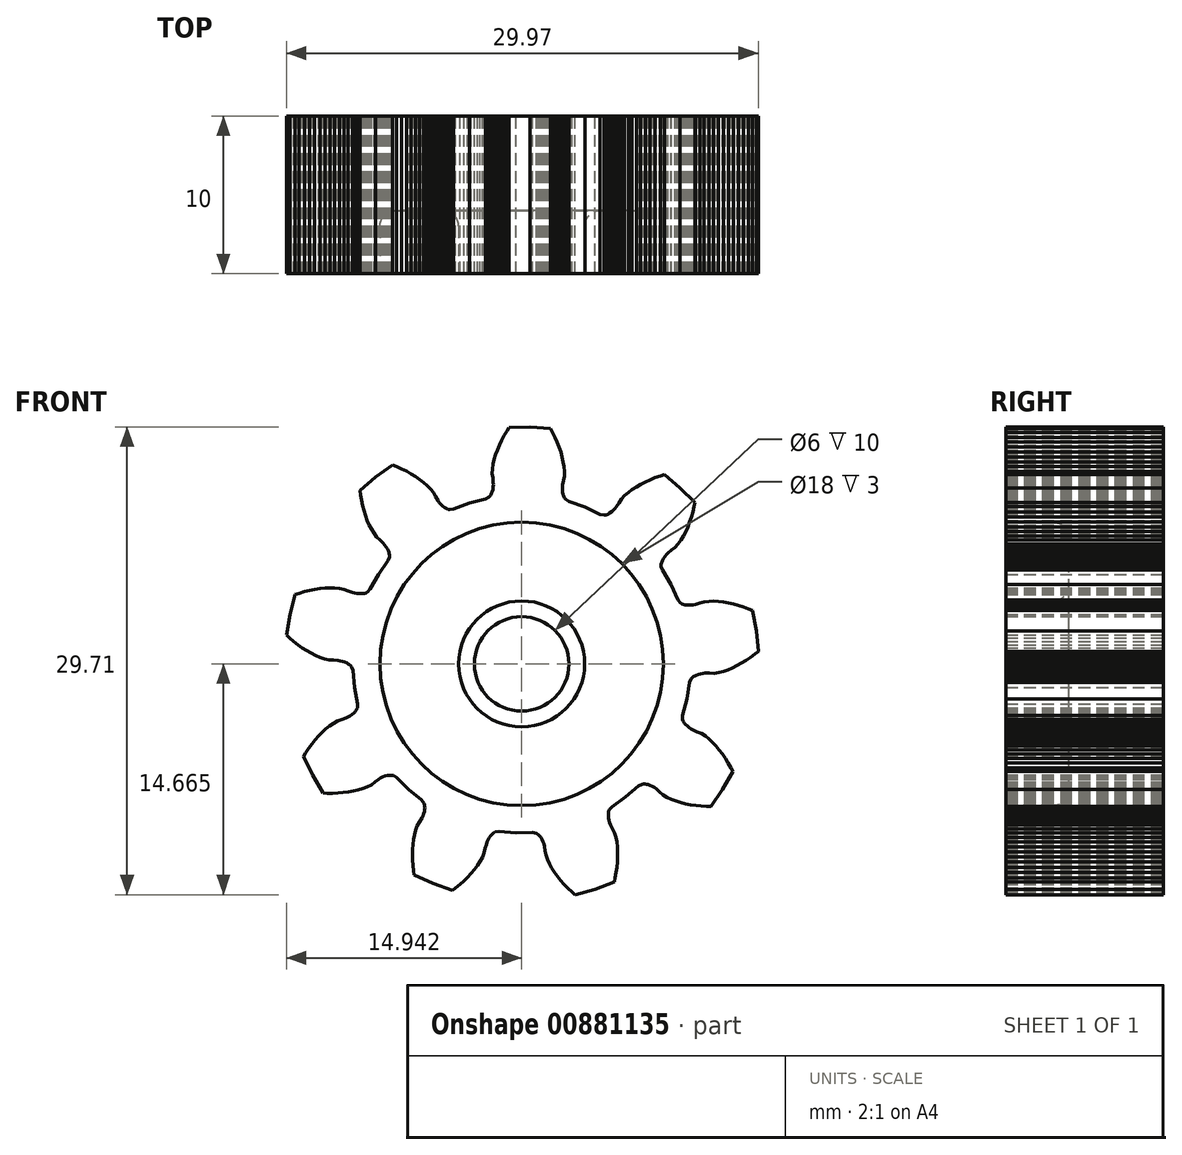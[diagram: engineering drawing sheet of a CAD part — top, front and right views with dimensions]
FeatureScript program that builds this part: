
annotation { "Feature Type Name" : "Feature", "Feature Type Description" : "" }
export const myFeature = defineFeature(function(context is Context, id is Id, definition is map)
    precondition{}
    {
        {
            var Q0;
            Q0=qCreatedBy(makeId("Front.planeOp"),FACE);
            var sketch = newSketch(context, id + "F0", { "sketchPlane" : qUnion([Q0])});
            skLineSegment(sketch, "E0", {"start": v(22.19, 0.3) * mm, "end": v(22.1, 0.53) * mm});
            skLineSegment(sketch, "E1", {"start": v(22.1, 0.53) * mm, "end": v(22.04, 0.62) * mm});
            skLineSegment(sketch, "E2", {"start": v(22.04, 0.62) * mm, "end": v(21.96, 0.69) * mm});
            skLineSegment(sketch, "E3", {"start": v(21.96, 0.69) * mm, "end": v(21.9, 0.74) * mm});
            skLineSegment(sketch, "E4", {"start": v(21.9, 0.74) * mm, "end": v(21.82, 0.78) * mm});
            skLineSegment(sketch, "E5", {"start": v(21.82, 0.78) * mm, "end": v(21.68, 0.85) * mm});
            skLineSegment(sketch, "E6", {"start": v(21.68, 0.85) * mm, "end": v(21.53, 0.9) * mm});
            skLineSegment(sketch, "E7", {"start": v(21.53, 0.9) * mm, "end": v(21.39, 0.93) * mm});
            skLineSegment(sketch, "E8", {"start": v(21.39, 0.93) * mm, "end": v(21.25, 0.95) * mm});
            skLineSegment(sketch, "E9", {"start": v(21.25, 0.95) * mm, "end": v(20.96, 0.97) * mm});
            skLineSegment(sketch, "E10", {"start": v(20.96, 0.97) * mm, "end": v(20.67, 0.98) * mm});
            skLineSegment(sketch, "E11", {"start": v(20.67, 0.98) * mm, "end": v(20.38, 1.05) * mm});
            skLineSegment(sketch, "E12", {"start": v(20.38, 1.05) * mm, "end": v(20.1, 1.15) * mm});
            skLineSegment(sketch, "E13", {"start": v(20.1, 1.15) * mm, "end": v(19.82, 1.27) * mm});
            skLineSegment(sketch, "E14", {"start": v(19.82, 1.27) * mm, "end": v(19.53, 1.4) * mm});
            skLineSegment(sketch, "E15", {"start": v(19.53, 1.4) * mm, "end": v(19.25, 1.57) * mm});
            skLineSegment(sketch, "E16", {"start": v(19.25, 1.57) * mm, "end": v(18.98, 1.75) * mm});
            skLineSegment(sketch, "E17", {"start": v(18.98, 1.75) * mm, "end": v(18.7, 1.94) * mm});
            skLineSegment(sketch, "E18", {"start": v(18.7, 1.94) * mm, "end": v(18.44, 2.15) * mm});
            skLineSegment(sketch, "E19", {"start": v(18.44, 2.15) * mm, "end": v(18.17, 2.38) * mm});
            skLineSegment(sketch, "E20", {"start": v(18.17, 2.38) * mm, "end": v(17.97, 2.56) * mm});
            skLineSegment(sketch, "E21", {"start": v(17.97, 2.56) * mm, "end": v(18.2, 3.85) * mm});
            skLineSegment(sketch, "E22", {"start": v(18.2, 3.85) * mm, "end": v(18.52, 5.13) * mm});
            skLineSegment(sketch, "E23", {"start": v(18.52, 5.13) * mm, "end": v(18.77, 5.21) * mm});
            skLineSegment(sketch, "E24", {"start": v(18.77, 5.21) * mm, "end": v(19.1, 5.31) * mm});
            skLineSegment(sketch, "E25", {"start": v(19.1, 5.31) * mm, "end": v(19.44, 5.4) * mm});
            skLineSegment(sketch, "E26", {"start": v(19.44, 5.4) * mm, "end": v(19.77, 5.46) * mm});
            skLineSegment(sketch, "E27", {"start": v(19.77, 5.46) * mm, "end": v(20.1, 5.51) * mm});
            skLineSegment(sketch, "E28", {"start": v(20.1, 5.51) * mm, "end": v(20.41, 5.54) * mm});
            skLineSegment(sketch, "E29", {"start": v(20.41, 5.54) * mm, "end": v(20.73, 5.56) * mm});
            skLineSegment(sketch, "E30", {"start": v(20.73, 5.56) * mm, "end": v(21.04, 5.55) * mm});
            skLineSegment(sketch, "E31", {"start": v(21.04, 5.55) * mm, "end": v(21.34, 5.52) * mm});
            skLineSegment(sketch, "E32", {"start": v(21.34, 5.52) * mm, "end": v(21.62, 5.47) * mm});
            skLineSegment(sketch, "E33", {"start": v(21.62, 5.47) * mm, "end": v(21.9, 5.36) * mm});
            skLineSegment(sketch, "E34", {"start": v(21.9, 5.36) * mm, "end": v(22.16, 5.27) * mm});
            skLineSegment(sketch, "E35", {"start": v(22.16, 5.27) * mm, "end": v(22.3, 5.23) * mm});
            skLineSegment(sketch, "E36", {"start": v(22.3, 5.23) * mm, "end": v(22.45, 5.2) * mm});
            skLineSegment(sketch, "E37", {"start": v(22.45, 5.2) * mm, "end": v(22.6, 5.19) * mm});
            skLineSegment(sketch, "E38", {"start": v(22.6, 5.19) * mm, "end": v(22.76, 5.19) * mm});
            skLineSegment(sketch, "E39", {"start": v(22.76, 5.19) * mm, "end": v(22.84, 5.2) * mm});
            skLineSegment(sketch, "E40", {"start": v(22.84, 5.2) * mm, "end": v(22.93, 5.21) * mm});
            skLineSegment(sketch, "E41", {"start": v(22.93, 5.21) * mm, "end": v(23.02, 5.24) * mm});
            skLineSegment(sketch, "E42", {"start": v(23.02, 5.24) * mm, "end": v(23.12, 5.3) * mm});
            skLineSegment(sketch, "E43", {"start": v(23.12, 5.3) * mm, "end": v(23.3, 5.48) * mm});
            skLineSegment(sketch, "E44", {"start": v(23.3, 5.48) * mm, "end": v(23.81, 6.41) * mm});
            skLineSegment(sketch, "E45", {"start": v(23.81, 6.41) * mm, "end": v(24.42, 7.29) * mm});
            skLineSegment(sketch, "E46", {"start": v(24.42, 7.29) * mm, "end": v(24.51, 7.52) * mm});
            skLineSegment(sketch, "E47", {"start": v(24.51, 7.52) * mm, "end": v(24.51, 7.64) * mm});
            skLineSegment(sketch, "E48", {"start": v(24.51, 7.64) * mm, "end": v(24.5, 7.73) * mm});
            skLineSegment(sketch, "E49", {"start": v(24.5, 7.73) * mm, "end": v(24.48, 7.82) * mm});
            skLineSegment(sketch, "E50", {"start": v(24.48, 7.82) * mm, "end": v(24.45, 7.9) * mm});
            skLineSegment(sketch, "E51", {"start": v(24.45, 7.9) * mm, "end": v(24.38, 8.04) * mm});
            skLineSegment(sketch, "E52", {"start": v(24.38, 8.04) * mm, "end": v(24.3, 8.17) * mm});
            skLineSegment(sketch, "E53", {"start": v(24.3, 8.17) * mm, "end": v(24.21, 8.29) * mm});
            skLineSegment(sketch, "E54", {"start": v(24.21, 8.29) * mm, "end": v(24.12, 8.4) * mm});
            skLineSegment(sketch, "E55", {"start": v(24.12, 8.4) * mm, "end": v(23.91, 8.6) * mm});
            skLineSegment(sketch, "E56", {"start": v(23.91, 8.6) * mm, "end": v(23.7, 8.8) * mm});
            skLineSegment(sketch, "E57", {"start": v(23.7, 8.8) * mm, "end": v(23.52, 9.03) * mm});
            skLineSegment(sketch, "E58", {"start": v(23.52, 9.03) * mm, "end": v(23.37, 9.28) * mm});
            skLineSegment(sketch, "E59", {"start": v(23.37, 9.28) * mm, "end": v(23.23, 9.56) * mm});
            skLineSegment(sketch, "E60", {"start": v(23.23, 9.56) * mm, "end": v(23.1, 9.85) * mm});
            skLineSegment(sketch, "E61", {"start": v(23.1, 9.85) * mm, "end": v(23, 10.15) * mm});
            skLineSegment(sketch, "E62", {"start": v(23, 10.15) * mm, "end": v(22.9, 10.46) * mm});
            skLineSegment(sketch, "E63", {"start": v(22.9, 10.46) * mm, "end": v(22.8, 10.79) * mm});
            skLineSegment(sketch, "E64", {"start": v(22.8, 10.79) * mm, "end": v(22.74, 11.12) * mm});
            skLineSegment(sketch, "E65", {"start": v(22.74, 11.12) * mm, "end": v(22.68, 11.47) * mm});
            skLineSegment(sketch, "E66", {"start": v(22.68, 11.47) * mm, "end": v(22.65, 11.73) * mm});
            skLineSegment(sketch, "E67", {"start": v(22.65, 11.73) * mm, "end": v(23.65, 12.59) * mm});
            skLineSegment(sketch, "E68", {"start": v(23.65, 12.59) * mm, "end": v(24.72, 13.35) * mm});
            skLineSegment(sketch, "E69", {"start": v(24.72, 13.35) * mm, "end": v(24.97, 13.25) * mm});
            skLineSegment(sketch, "E70", {"start": v(24.97, 13.25) * mm, "end": v(25.29, 13.11) * mm});
            skLineSegment(sketch, "E71", {"start": v(25.29, 13.11) * mm, "end": v(25.6, 12.96) * mm});
            skLineSegment(sketch, "E72", {"start": v(25.6, 12.96) * mm, "end": v(25.89, 12.8) * mm});
            skLineSegment(sketch, "E73", {"start": v(25.89, 12.8) * mm, "end": v(26.17, 12.63) * mm});
            skLineSegment(sketch, "E74", {"start": v(26.17, 12.63) * mm, "end": v(26.43, 12.45) * mm});
            skLineSegment(sketch, "E75", {"start": v(26.43, 12.45) * mm, "end": v(26.68, 12.26) * mm});
            skLineSegment(sketch, "E76", {"start": v(26.68, 12.26) * mm, "end": v(26.92, 12.06) * mm});
            skLineSegment(sketch, "E77", {"start": v(26.92, 12.06) * mm, "end": v(27.13, 11.84) * mm});
            skLineSegment(sketch, "E78", {"start": v(27.13, 11.84) * mm, "end": v(27.31, 11.61) * mm});
            skLineSegment(sketch, "E79", {"start": v(27.31, 11.61) * mm, "end": v(27.45, 11.36) * mm});
            skLineSegment(sketch, "E80", {"start": v(27.45, 11.36) * mm, "end": v(27.6, 11.11) * mm});
            skLineSegment(sketch, "E81", {"start": v(27.6, 11.11) * mm, "end": v(27.68, 11) * mm});
            skLineSegment(sketch, "E82", {"start": v(27.68, 11) * mm, "end": v(27.77, 10.88) * mm});
            skLineSegment(sketch, "E83", {"start": v(27.77, 10.88) * mm, "end": v(27.88, 10.77) * mm});
            skLineSegment(sketch, "E84", {"start": v(27.88, 10.77) * mm, "end": v(28, 10.67) * mm});
            skLineSegment(sketch, "E85", {"start": v(28, 10.67) * mm, "end": v(28.07, 10.63) * mm});
            skLineSegment(sketch, "E86", {"start": v(28.07, 10.63) * mm, "end": v(28.15, 10.58) * mm});
            skLineSegment(sketch, "E87", {"start": v(28.15, 10.58) * mm, "end": v(28.24, 10.55) * mm});
            skLineSegment(sketch, "E88", {"start": v(28.24, 10.55) * mm, "end": v(28.35, 10.52) * mm});
            skLineSegment(sketch, "E89", {"start": v(28.35, 10.52) * mm, "end": v(28.6, 10.55) * mm});
            skLineSegment(sketch, "E90", {"start": v(28.6, 10.55) * mm, "end": v(29.6, 10.93) * mm});
            skLineSegment(sketch, "E91", {"start": v(29.6, 10.93) * mm, "end": v(30.63, 11.21) * mm});
            skLineSegment(sketch, "E92", {"start": v(30.63, 11.21) * mm, "end": v(30.84, 11.33) * mm});
            skLineSegment(sketch, "E93", {"start": v(30.84, 11.33) * mm, "end": v(30.92, 11.42) * mm});
            skLineSegment(sketch, "E94", {"start": v(30.92, 11.42) * mm, "end": v(30.97, 11.5) * mm});
            skLineSegment(sketch, "E95", {"start": v(30.97, 11.5) * mm, "end": v(31.01, 11.58) * mm});
            skLineSegment(sketch, "E96", {"start": v(31.01, 11.58) * mm, "end": v(31.04, 11.66) * mm});
            skLineSegment(sketch, "E97", {"start": v(31.04, 11.66) * mm, "end": v(31.08, 11.81) * mm});
            skLineSegment(sketch, "E98", {"start": v(31.08, 11.81) * mm, "end": v(31.1, 11.96) * mm});
            skLineSegment(sketch, "E99", {"start": v(31.1, 11.96) * mm, "end": v(31.1, 12.1) * mm});
            skLineSegment(sketch, "E100", {"start": v(31.1, 12.1) * mm, "end": v(31.1, 12.25) * mm});
            skLineSegment(sketch, "E101", {"start": v(31.1, 12.25) * mm, "end": v(31.08, 12.54) * mm});
            skLineSegment(sketch, "E102", {"start": v(31.08, 12.54) * mm, "end": v(31.04, 12.83) * mm});
            skLineSegment(sketch, "E103", {"start": v(31.04, 12.83) * mm, "end": v(31.06, 13.12) * mm});
            skLineSegment(sketch, "E104", {"start": v(31.06, 13.12) * mm, "end": v(31.1, 13.42) * mm});
            skLineSegment(sketch, "E105", {"start": v(31.1, 13.42) * mm, "end": v(31.17, 13.72) * mm});
            skLineSegment(sketch, "E106", {"start": v(31.17, 13.72) * mm, "end": v(31.26, 14.02) * mm});
            skLineSegment(sketch, "E107", {"start": v(31.26, 14.02) * mm, "end": v(31.37, 14.32) * mm});
            skLineSegment(sketch, "E108", {"start": v(31.37, 14.32) * mm, "end": v(31.5, 14.62) * mm});
            skLineSegment(sketch, "E109", {"start": v(31.5, 14.62) * mm, "end": v(31.64, 14.93) * mm});
            skLineSegment(sketch, "E110", {"start": v(31.64, 14.93) * mm, "end": v(31.8, 15.23) * mm});
            skLineSegment(sketch, "E111", {"start": v(31.8, 15.23) * mm, "end": v(31.98, 15.53) * mm});
            skLineSegment(sketch, "E112", {"start": v(31.98, 15.53) * mm, "end": v(32.12, 15.76) * mm});
            skLineSegment(sketch, "E113", {"start": v(32.12, 15.76) * mm, "end": v(33.44, 15.77) * mm});
            skLineSegment(sketch, "E114", {"start": v(33.44, 15.77) * mm, "end": v(34.75, 15.66) * mm});
            skLineSegment(sketch, "E115", {"start": v(34.75, 15.66) * mm, "end": v(34.88, 15.43) * mm});
            skLineSegment(sketch, "E116", {"start": v(34.88, 15.43) * mm, "end": v(35.03, 15.12) * mm});
            skLineSegment(sketch, "E117", {"start": v(35.03, 15.12) * mm, "end": v(35.17, 14.8) * mm});
            skLineSegment(sketch, "E118", {"start": v(35.17, 14.8) * mm, "end": v(35.3, 14.5) * mm});
            skLineSegment(sketch, "E119", {"start": v(35.3, 14.5) * mm, "end": v(35.4, 14.18) * mm});
            skLineSegment(sketch, "E120", {"start": v(35.4, 14.18) * mm, "end": v(35.49, 13.87) * mm});
            skLineSegment(sketch, "E121", {"start": v(35.49, 13.87) * mm, "end": v(35.55, 13.56) * mm});
            skLineSegment(sketch, "E122", {"start": v(35.55, 13.56) * mm, "end": v(35.6, 13.26) * mm});
            skLineSegment(sketch, "E123", {"start": v(35.6, 13.26) * mm, "end": v(35.63, 12.96) * mm});
            skLineSegment(sketch, "E124", {"start": v(35.63, 12.96) * mm, "end": v(35.62, 12.67) * mm});
            skLineSegment(sketch, "E125", {"start": v(35.62, 12.67) * mm, "end": v(35.57, 12.38) * mm});
            skLineSegment(sketch, "E126", {"start": v(35.57, 12.38) * mm, "end": v(35.52, 12.1) * mm});
            skLineSegment(sketch, "E127", {"start": v(35.52, 12.1) * mm, "end": v(35.5, 11.95) * mm});
            skLineSegment(sketch, "E128", {"start": v(35.5, 11.95) * mm, "end": v(35.5, 11.8) * mm});
            skLineSegment(sketch, "E129", {"start": v(35.5, 11.8) * mm, "end": v(35.51, 11.66) * mm});
            skLineSegment(sketch, "E130", {"start": v(35.51, 11.66) * mm, "end": v(35.54, 11.5) * mm});
            skLineSegment(sketch, "E131", {"start": v(35.54, 11.5) * mm, "end": v(35.57, 11.42) * mm});
            skLineSegment(sketch, "E132", {"start": v(35.57, 11.42) * mm, "end": v(35.6, 11.34) * mm});
            skLineSegment(sketch, "E133", {"start": v(35.6, 11.34) * mm, "end": v(35.64, 11.25) * mm});
            skLineSegment(sketch, "E134", {"start": v(35.64, 11.25) * mm, "end": v(35.71, 11.16) * mm});
            skLineSegment(sketch, "E135", {"start": v(35.71, 11.16) * mm, "end": v(35.92, 11.03) * mm});
            skLineSegment(sketch, "E136", {"start": v(35.92, 11.03) * mm, "end": v(36.93, 10.68) * mm});
            skLineSegment(sketch, "E137", {"start": v(36.93, 10.68) * mm, "end": v(37.9, 10.23) * mm});
            skLineSegment(sketch, "E138", {"start": v(37.9, 10.23) * mm, "end": v(38.14, 10.18) * mm});
            skLineSegment(sketch, "E139", {"start": v(38.14, 10.18) * mm, "end": v(38.26, 10.2) * mm});
            skLineSegment(sketch, "E140", {"start": v(38.26, 10.2) * mm, "end": v(38.35, 10.23) * mm});
            skLineSegment(sketch, "E141", {"start": v(38.35, 10.23) * mm, "end": v(38.43, 10.26) * mm});
            skLineSegment(sketch, "E142", {"start": v(38.43, 10.26) * mm, "end": v(38.5, 10.3) * mm});
            skLineSegment(sketch, "E143", {"start": v(38.5, 10.3) * mm, "end": v(38.63, 10.4) * mm});
            skLineSegment(sketch, "E144", {"start": v(38.63, 10.4) * mm, "end": v(38.75, 10.5) * mm});
            skLineSegment(sketch, "E145", {"start": v(38.75, 10.5) * mm, "end": v(38.85, 10.6) * mm});
            skLineSegment(sketch, "E146", {"start": v(38.85, 10.6) * mm, "end": v(38.94, 10.72) * mm});
            skLineSegment(sketch, "E147", {"start": v(38.94, 10.72) * mm, "end": v(39.1, 10.96) * mm});
            skLineSegment(sketch, "E148", {"start": v(39.1, 10.96) * mm, "end": v(39.26, 11.2) * mm});
            skLineSegment(sketch, "E149", {"start": v(39.26, 11.2) * mm, "end": v(39.46, 11.41) * mm});
            skLineSegment(sketch, "E150", {"start": v(39.46, 11.41) * mm, "end": v(39.68, 11.61) * mm});
            skLineSegment(sketch, "E151", {"start": v(39.68, 11.61) * mm, "end": v(39.93, 11.8) * mm});
            skLineSegment(sketch, "E152", {"start": v(39.93, 11.8) * mm, "end": v(40.2, 11.97) * mm});
            skLineSegment(sketch, "E153", {"start": v(40.2, 11.97) * mm, "end": v(40.47, 12.13) * mm});
            skLineSegment(sketch, "E154", {"start": v(40.47, 12.13) * mm, "end": v(40.76, 12.28) * mm});
            skLineSegment(sketch, "E155", {"start": v(40.76, 12.28) * mm, "end": v(41.07, 12.42) * mm});
            skLineSegment(sketch, "E156", {"start": v(41.07, 12.42) * mm, "end": v(41.38, 12.55) * mm});
            skLineSegment(sketch, "E157", {"start": v(41.38, 12.55) * mm, "end": v(41.71, 12.67) * mm});
            skLineSegment(sketch, "E158", {"start": v(41.71, 12.67) * mm, "end": v(41.97, 12.75) * mm});
            skLineSegment(sketch, "E159", {"start": v(41.97, 12.75) * mm, "end": v(42.98, 11.91) * mm});
            skLineSegment(sketch, "E160", {"start": v(42.98, 11.91) * mm, "end": v(43.92, 10.99) * mm});
            skLineSegment(sketch, "E161", {"start": v(43.92, 10.99) * mm, "end": v(43.87, 10.73) * mm});
            skLineSegment(sketch, "E162", {"start": v(43.87, 10.73) * mm, "end": v(43.79, 10.39) * mm});
            skLineSegment(sketch, "E163", {"start": v(43.79, 10.39) * mm, "end": v(43.7, 10.06) * mm});
            skLineSegment(sketch, "E164", {"start": v(43.7, 10.06) * mm, "end": v(43.59, 9.74) * mm});
            skLineSegment(sketch, "E165", {"start": v(43.59, 9.74) * mm, "end": v(43.47, 9.43) * mm});
            skLineSegment(sketch, "E166", {"start": v(43.47, 9.43) * mm, "end": v(43.33, 9.14) * mm});
            skLineSegment(sketch, "E167", {"start": v(43.33, 9.14) * mm, "end": v(43.19, 8.86) * mm});
            skLineSegment(sketch, "E168", {"start": v(43.19, 8.86) * mm, "end": v(43.03, 8.6) * mm});
            skLineSegment(sketch, "E169", {"start": v(43.03, 8.6) * mm, "end": v(42.86, 8.35) * mm});
            skLineSegment(sketch, "E170", {"start": v(42.86, 8.35) * mm, "end": v(42.66, 8.13) * mm});
            skLineSegment(sketch, "E171", {"start": v(42.66, 8.13) * mm, "end": v(42.44, 7.95) * mm});
            skLineSegment(sketch, "E172", {"start": v(42.44, 7.95) * mm, "end": v(42.22, 7.76) * mm});
            skLineSegment(sketch, "E173", {"start": v(42.22, 7.76) * mm, "end": v(42.12, 7.66) * mm});
            skLineSegment(sketch, "E174", {"start": v(42.12, 7.66) * mm, "end": v(42.02, 7.55) * mm});
            skLineSegment(sketch, "E175", {"start": v(42.02, 7.55) * mm, "end": v(41.93, 7.43) * mm});
            skLineSegment(sketch, "E176", {"start": v(41.93, 7.43) * mm, "end": v(41.85, 7.29) * mm});
            skLineSegment(sketch, "E177", {"start": v(41.85, 7.29) * mm, "end": v(41.82, 7.21) * mm});
            skLineSegment(sketch, "E178", {"start": v(41.82, 7.21) * mm, "end": v(41.8, 7.13) * mm});
            skLineSegment(sketch, "E179", {"start": v(41.8, 7.13) * mm, "end": v(41.77, 7.03) * mm});
            skLineSegment(sketch, "E180", {"start": v(41.77, 7.03) * mm, "end": v(41.77, 6.92) * mm});
            skLineSegment(sketch, "E181", {"start": v(41.77, 6.92) * mm, "end": v(41.84, 6.68) * mm});
            skLineSegment(sketch, "E182", {"start": v(41.84, 6.68) * mm, "end": v(42.39, 5.76) * mm});
            skLineSegment(sketch, "E183", {"start": v(42.39, 5.76) * mm, "end": v(42.84, 4.8) * mm});
            skLineSegment(sketch, "E184", {"start": v(42.84, 4.8) * mm, "end": v(43, 4.6) * mm});
            skLineSegment(sketch, "E185", {"start": v(43, 4.6) * mm, "end": v(43.1, 4.54) * mm});
            skLineSegment(sketch, "E186", {"start": v(43.1, 4.54) * mm, "end": v(43.19, 4.5) * mm});
            skLineSegment(sketch, "E187", {"start": v(43.19, 4.5) * mm, "end": v(43.27, 4.48) * mm});
            skLineSegment(sketch, "E188", {"start": v(43.27, 4.48) * mm, "end": v(43.35, 4.47) * mm});
            skLineSegment(sketch, "E189", {"start": v(43.35, 4.47) * mm, "end": v(43.51, 4.46) * mm});
            skLineSegment(sketch, "E190", {"start": v(43.51, 4.46) * mm, "end": v(43.66, 4.46) * mm});
            skLineSegment(sketch, "E191", {"start": v(43.66, 4.46) * mm, "end": v(43.8, 4.48) * mm});
            skLineSegment(sketch, "E192", {"start": v(43.8, 4.48) * mm, "end": v(43.95, 4.5) * mm});
            skLineSegment(sketch, "E193", {"start": v(43.95, 4.5) * mm, "end": v(44.23, 4.58) * mm});
            skLineSegment(sketch, "E194", {"start": v(44.23, 4.58) * mm, "end": v(44.5, 4.67) * mm});
            skLineSegment(sketch, "E195", {"start": v(44.5, 4.67) * mm, "end": v(44.8, 4.7) * mm});
            skLineSegment(sketch, "E196", {"start": v(44.8, 4.7) * mm, "end": v(45.1, 4.71) * mm});
            skLineSegment(sketch, "E197", {"start": v(45.1, 4.71) * mm, "end": v(45.4, 4.7) * mm});
            skLineSegment(sketch, "E198", {"start": v(45.4, 4.7) * mm, "end": v(45.72, 4.66) * mm});
            skLineSegment(sketch, "E199", {"start": v(45.72, 4.66) * mm, "end": v(46.03, 4.6) * mm});
            skLineSegment(sketch, "E200", {"start": v(46.03, 4.6) * mm, "end": v(46.35, 4.53) * mm});
            skLineSegment(sketch, "E201", {"start": v(46.35, 4.53) * mm, "end": v(46.68, 4.44) * mm});
            skLineSegment(sketch, "E202", {"start": v(46.68, 4.44) * mm, "end": v(47, 4.34) * mm});
            skLineSegment(sketch, "E203", {"start": v(47, 4.34) * mm, "end": v(47.33, 4.22) * mm});
            skLineSegment(sketch, "E204", {"start": v(47.33, 4.22) * mm, "end": v(47.58, 4.11) * mm});
            skLineSegment(sketch, "E205", {"start": v(47.58, 4.11) * mm, "end": v(47.82, 2.82) * mm});
            skLineSegment(sketch, "E206", {"start": v(47.82, 2.82) * mm, "end": v(47.94, 1.51) * mm});
            skLineSegment(sketch, "E207", {"start": v(47.94, 1.51) * mm, "end": v(47.73, 1.34) * mm});
            skLineSegment(sketch, "E208", {"start": v(47.73, 1.34) * mm, "end": v(47.45, 1.14) * mm});
            skLineSegment(sketch, "E209", {"start": v(47.45, 1.14) * mm, "end": v(47.17, 0.95) * mm});
            skLineSegment(sketch, "E210", {"start": v(47.17, 0.95) * mm, "end": v(46.88, 0.77) * mm});
            skLineSegment(sketch, "E211", {"start": v(46.88, 0.77) * mm, "end": v(46.6, 0.61) * mm});
            skLineSegment(sketch, "E212", {"start": v(46.6, 0.61) * mm, "end": v(46.3, 0.47) * mm});
            skLineSegment(sketch, "E213", {"start": v(46.3, 0.47) * mm, "end": v(46.01, 0.35) * mm});
            skLineSegment(sketch, "E214", {"start": v(46.01, 0.35) * mm, "end": v(45.72, 0.25) * mm});
            skLineSegment(sketch, "E215", {"start": v(45.72, 0.25) * mm, "end": v(45.43, 0.18) * mm});
            skLineSegment(sketch, "E216", {"start": v(45.43, 0.18) * mm, "end": v(45.14, 0.13) * mm});
            skLineSegment(sketch, "E217", {"start": v(45.14, 0.13) * mm, "end": v(44.85, 0.14) * mm});
            skLineSegment(sketch, "E218", {"start": v(44.85, 0.14) * mm, "end": v(44.57, 0.14) * mm});
            skLineSegment(sketch, "E219", {"start": v(44.57, 0.14) * mm, "end": v(44.42, 0.12) * mm});
            skLineSegment(sketch, "E220", {"start": v(44.42, 0.12) * mm, "end": v(44.27, 0.1) * mm});
            skLineSegment(sketch, "E221", {"start": v(44.27, 0.1) * mm, "end": v(44.13, 0.06) * mm});
            skLineSegment(sketch, "E222", {"start": v(44.13, 0.06) * mm, "end": v(43.98, 0) * mm});
            skLineSegment(sketch, "E223", {"start": v(43.98, 0) * mm, "end": v(43.9, -0.03) * mm});
            skLineSegment(sketch, "E224", {"start": v(43.9, -0.03) * mm, "end": v(43.83, -0.08) * mm});
            skLineSegment(sketch, "E225", {"start": v(43.83, -0.08) * mm, "end": v(43.75, -0.14) * mm});
            skLineSegment(sketch, "E226", {"start": v(43.75, -0.14) * mm, "end": v(43.67, -0.22) * mm});
            skLineSegment(sketch, "E227", {"start": v(43.67, -0.22) * mm, "end": v(43.58, -0.45) * mm});
            skLineSegment(sketch, "E228", {"start": v(43.58, -0.45) * mm, "end": v(43.4, -1.5) * mm});
            skLineSegment(sketch, "E229", {"start": v(43.4, -1.5) * mm, "end": v(43.14, -2.54) * mm});
            skLineSegment(sketch, "E230", {"start": v(43.14, -2.54) * mm, "end": v(43.13, -2.79) * mm});
            skLineSegment(sketch, "E231", {"start": v(43.13, -2.79) * mm, "end": v(43.17, -2.9) * mm});
            skLineSegment(sketch, "E232", {"start": v(43.17, -2.9) * mm, "end": v(43.21, -2.98) * mm});
            skLineSegment(sketch, "E233", {"start": v(43.21, -2.98) * mm, "end": v(43.26, -3.06) * mm});
            skLineSegment(sketch, "E234", {"start": v(43.26, -3.06) * mm, "end": v(43.32, -3.12) * mm});
            skLineSegment(sketch, "E235", {"start": v(43.32, -3.12) * mm, "end": v(43.43, -3.23) * mm});
            skLineSegment(sketch, "E236", {"start": v(43.43, -3.23) * mm, "end": v(43.55, -3.32) * mm});
            skLineSegment(sketch, "E237", {"start": v(43.55, -3.32) * mm, "end": v(43.67, -3.4) * mm});
            skLineSegment(sketch, "E238", {"start": v(43.67, -3.4) * mm, "end": v(43.8, -3.48) * mm});
            skLineSegment(sketch, "E239", {"start": v(43.8, -3.48) * mm, "end": v(44.06, -3.6) * mm});
            skLineSegment(sketch, "E240", {"start": v(44.06, -3.6) * mm, "end": v(44.33, -3.7) * mm});
            skLineSegment(sketch, "E241", {"start": v(44.33, -3.7) * mm, "end": v(44.57, -3.86) * mm});
            skLineSegment(sketch, "E242", {"start": v(44.57, -3.86) * mm, "end": v(44.8, -4.05) * mm});
            skLineSegment(sketch, "E243", {"start": v(44.8, -4.05) * mm, "end": v(45.03, -4.26) * mm});
            skLineSegment(sketch, "E244", {"start": v(45.03, -4.26) * mm, "end": v(45.25, -4.5) * mm});
            skLineSegment(sketch, "E245", {"start": v(45.25, -4.5) * mm, "end": v(45.46, -4.74) * mm});
            skLineSegment(sketch, "E246", {"start": v(45.46, -4.74) * mm, "end": v(45.66, -5) * mm});
            skLineSegment(sketch, "E247", {"start": v(45.66, -5) * mm, "end": v(45.85, -5.27) * mm});
            skLineSegment(sketch, "E248", {"start": v(45.85, -5.27) * mm, "end": v(46.03, -5.56) * mm});
            skLineSegment(sketch, "E249", {"start": v(46.03, -5.56) * mm, "end": v(46.2, -5.87) * mm});
            skLineSegment(sketch, "E250", {"start": v(46.2, -5.87) * mm, "end": v(46.32, -6.1) * mm});
            skLineSegment(sketch, "E251", {"start": v(46.32, -6.1) * mm, "end": v(45.68, -7.25) * mm});
            skLineSegment(sketch, "E252", {"start": v(45.68, -7.25) * mm, "end": v(44.93, -8.33) * mm});
            skLineSegment(sketch, "E253", {"start": v(44.93, -8.33) * mm, "end": v(44.66, -8.33) * mm});
            skLineSegment(sketch, "E254", {"start": v(44.66, -8.33) * mm, "end": v(44.32, -8.3) * mm});
            skLineSegment(sketch, "E255", {"start": v(44.32, -8.3) * mm, "end": v(43.98, -8.27) * mm});
            skLineSegment(sketch, "E256", {"start": v(43.98, -8.27) * mm, "end": v(43.64, -8.22) * mm});
            skLineSegment(sketch, "E257", {"start": v(43.64, -8.22) * mm, "end": v(43.32, -8.16) * mm});
            skLineSegment(sketch, "E258", {"start": v(43.32, -8.16) * mm, "end": v(43, -8.08) * mm});
            skLineSegment(sketch, "E259", {"start": v(43, -8.08) * mm, "end": v(42.7, -7.98) * mm});
            skLineSegment(sketch, "E260", {"start": v(42.7, -7.98) * mm, "end": v(42.42, -7.87) * mm});
            skLineSegment(sketch, "E261", {"start": v(42.42, -7.87) * mm, "end": v(42.15, -7.74) * mm});
            skLineSegment(sketch, "E262", {"start": v(42.15, -7.74) * mm, "end": v(41.9, -7.6) * mm});
            skLineSegment(sketch, "E263", {"start": v(41.9, -7.6) * mm, "end": v(41.68, -7.4) * mm});
            skLineSegment(sketch, "E264", {"start": v(41.68, -7.4) * mm, "end": v(41.46, -7.22) * mm});
            skLineSegment(sketch, "E265", {"start": v(41.46, -7.22) * mm, "end": v(41.34, -7.13) * mm});
            skLineSegment(sketch, "E266", {"start": v(41.34, -7.13) * mm, "end": v(41.21, -7.06) * mm});
            skLineSegment(sketch, "E267", {"start": v(41.21, -7.06) * mm, "end": v(41.08, -7) * mm});
            skLineSegment(sketch, "E268", {"start": v(41.08, -7) * mm, "end": v(40.93, -6.94) * mm});
            skLineSegment(sketch, "E269", {"start": v(40.93, -6.94) * mm, "end": v(40.85, -6.92) * mm});
            skLineSegment(sketch, "E270", {"start": v(40.85, -6.92) * mm, "end": v(40.76, -6.9) * mm});
            skLineSegment(sketch, "E271", {"start": v(40.76, -6.9) * mm, "end": v(40.66, -6.9) * mm});
            skLineSegment(sketch, "E272", {"start": v(40.66, -6.9) * mm, "end": v(40.55, -6.92) * mm});
            skLineSegment(sketch, "E273", {"start": v(40.55, -6.92) * mm, "end": v(40.33, -7.03) * mm});
            skLineSegment(sketch, "E274", {"start": v(40.33, -7.03) * mm, "end": v(39.52, -7.73) * mm});
            skLineSegment(sketch, "E275", {"start": v(39.52, -7.73) * mm, "end": v(38.65, -8.35) * mm});
            skLineSegment(sketch, "E276", {"start": v(38.65, -8.35) * mm, "end": v(38.48, -8.53) * mm});
            skLineSegment(sketch, "E277", {"start": v(38.48, -8.53) * mm, "end": v(38.44, -8.64) * mm});
            skLineSegment(sketch, "E278", {"start": v(38.44, -8.64) * mm, "end": v(38.42, -8.74) * mm});
            skLineSegment(sketch, "E279", {"start": v(38.42, -8.74) * mm, "end": v(38.41, -8.82) * mm});
            skLineSegment(sketch, "E280", {"start": v(38.41, -8.82) * mm, "end": v(38.41, -8.9) * mm});
            skLineSegment(sketch, "E281", {"start": v(38.41, -8.9) * mm, "end": v(38.43, -9.06) * mm});
            skLineSegment(sketch, "E282", {"start": v(38.43, -9.06) * mm, "end": v(38.46, -9.21) * mm});
            skLineSegment(sketch, "E283", {"start": v(38.46, -9.21) * mm, "end": v(38.5, -9.35) * mm});
            skLineSegment(sketch, "E284", {"start": v(38.5, -9.35) * mm, "end": v(38.55, -9.49) * mm});
            skLineSegment(sketch, "E285", {"start": v(38.55, -9.49) * mm, "end": v(38.68, -9.75) * mm});
            skLineSegment(sketch, "E286", {"start": v(38.68, -9.75) * mm, "end": v(38.8, -10) * mm});
            skLineSegment(sketch, "E287", {"start": v(38.8, -10) * mm, "end": v(38.9, -10.29) * mm});
            skLineSegment(sketch, "E288", {"start": v(38.9, -10.29) * mm, "end": v(38.95, -10.58) * mm});
            skLineSegment(sketch, "E289", {"start": v(38.95, -10.58) * mm, "end": v(39, -10.89) * mm});
            skLineSegment(sketch, "E290", {"start": v(39, -10.89) * mm, "end": v(39, -11.2) * mm});
            skLineSegment(sketch, "E291", {"start": v(39, -11.2) * mm, "end": v(39.01, -11.52) * mm});
            skLineSegment(sketch, "E292", {"start": v(39.01, -11.52) * mm, "end": v(39, -11.85) * mm});
            skLineSegment(sketch, "E293", {"start": v(39, -11.85) * mm, "end": v(38.96, -12.19) * mm});
            skLineSegment(sketch, "E294", {"start": v(38.96, -12.19) * mm, "end": v(38.92, -12.52) * mm});
            skLineSegment(sketch, "E295", {"start": v(38.92, -12.52) * mm, "end": v(38.85, -12.87) * mm});
            skLineSegment(sketch, "E296", {"start": v(38.85, -12.87) * mm, "end": v(38.8, -13.13) * mm});
            skLineSegment(sketch, "E297", {"start": v(38.8, -13.13) * mm, "end": v(37.56, -13.59) * mm});
            skLineSegment(sketch, "E298", {"start": v(37.56, -13.59) * mm, "end": v(36.3, -13.94) * mm});
            skLineSegment(sketch, "E299", {"start": v(36.3, -13.94) * mm, "end": v(36.1, -13.76) * mm});
            skLineSegment(sketch, "E300", {"start": v(36.1, -13.76) * mm, "end": v(35.84, -13.52) * mm});
            skLineSegment(sketch, "E301", {"start": v(35.84, -13.52) * mm, "end": v(35.6, -13.28) * mm});
            skLineSegment(sketch, "E302", {"start": v(35.6, -13.28) * mm, "end": v(35.38, -13.03) * mm});
            skLineSegment(sketch, "E303", {"start": v(35.38, -13.03) * mm, "end": v(35.18, -12.77) * mm});
            skLineSegment(sketch, "E304", {"start": v(35.18, -12.77) * mm, "end": v(34.99, -12.5) * mm});
            skLineSegment(sketch, "E305", {"start": v(34.99, -12.5) * mm, "end": v(34.82, -12.24) * mm});
            skLineSegment(sketch, "E306", {"start": v(34.82, -12.24) * mm, "end": v(34.67, -11.97) * mm});
            skLineSegment(sketch, "E307", {"start": v(34.67, -11.97) * mm, "end": v(34.54, -11.7) * mm});
            skLineSegment(sketch, "E308", {"start": v(34.54, -11.7) * mm, "end": v(34.45, -11.42) * mm});
            skLineSegment(sketch, "E309", {"start": v(34.45, -11.42) * mm, "end": v(34.4, -11.14) * mm});
            skLineSegment(sketch, "E310", {"start": v(34.4, -11.14) * mm, "end": v(34.35, -10.85) * mm});
            skLineSegment(sketch, "E311", {"start": v(34.35, -10.85) * mm, "end": v(34.32, -10.71) * mm});
            skLineSegment(sketch, "E312", {"start": v(34.32, -10.71) * mm, "end": v(34.27, -10.57) * mm});
            skLineSegment(sketch, "E313", {"start": v(34.27, -10.57) * mm, "end": v(34.2, -10.44) * mm});
            skLineSegment(sketch, "E314", {"start": v(34.2, -10.44) * mm, "end": v(34.13, -10.3) * mm});
            skLineSegment(sketch, "E315", {"start": v(34.13, -10.3) * mm, "end": v(34.08, -10.23) * mm});
            skLineSegment(sketch, "E316", {"start": v(34.08, -10.23) * mm, "end": v(34.02, -10.17) * mm});
            skLineSegment(sketch, "E317", {"start": v(34.02, -10.17) * mm, "end": v(33.94, -10.1) * mm});
            skLineSegment(sketch, "E318", {"start": v(33.94, -10.1) * mm, "end": v(33.85, -10.04) * mm});
            skLineSegment(sketch, "E319", {"start": v(33.85, -10.04) * mm, "end": v(33.6, -9.98) * mm});
            skLineSegment(sketch, "E320", {"start": v(33.6, -9.98) * mm, "end": v(32.54, -10) * mm});
            skLineSegment(sketch, "E321", {"start": v(32.54, -10) * mm, "end": v(31.47, -9.91) * mm});
            skLineSegment(sketch, "E322", {"start": v(31.47, -9.91) * mm, "end": v(31.23, -9.95) * mm});
            skLineSegment(sketch, "E323", {"start": v(31.23, -9.95) * mm, "end": v(31.13, -10) * mm});
            skLineSegment(sketch, "E324", {"start": v(31.13, -10) * mm, "end": v(31.05, -10.06) * mm});
            skLineSegment(sketch, "E325", {"start": v(31.05, -10.06) * mm, "end": v(30.99, -10.13) * mm});
            skLineSegment(sketch, "E326", {"start": v(30.99, -10.13) * mm, "end": v(30.93, -10.19) * mm});
            skLineSegment(sketch, "E327", {"start": v(30.93, -10.19) * mm, "end": v(30.84, -10.32) * mm});
            skLineSegment(sketch, "E328", {"start": v(30.84, -10.32) * mm, "end": v(30.77, -10.45) * mm});
            skLineSegment(sketch, "E329", {"start": v(30.77, -10.45) * mm, "end": v(30.71, -10.59) * mm});
            skLineSegment(sketch, "E330", {"start": v(30.71, -10.59) * mm, "end": v(30.67, -10.72) * mm});
            skLineSegment(sketch, "E331", {"start": v(30.67, -10.72) * mm, "end": v(30.6, -11) * mm});
            skLineSegment(sketch, "E332", {"start": v(30.6, -11) * mm, "end": v(30.53, -11.28) * mm});
            skLineSegment(sketch, "E333", {"start": v(30.53, -11.28) * mm, "end": v(30.42, -11.56) * mm});
            skLineSegment(sketch, "E334", {"start": v(30.42, -11.56) * mm, "end": v(30.27, -11.82) * mm});
            skLineSegment(sketch, "E335", {"start": v(30.27, -11.82) * mm, "end": v(30.1, -12.08) * mm});
            skLineSegment(sketch, "E336", {"start": v(30.1, -12.08) * mm, "end": v(29.92, -12.33) * mm});
            skLineSegment(sketch, "E337", {"start": v(29.92, -12.33) * mm, "end": v(29.71, -12.58) * mm});
            skLineSegment(sketch, "E338", {"start": v(29.71, -12.58) * mm, "end": v(29.49, -12.82) * mm});
            skLineSegment(sketch, "E339", {"start": v(29.49, -12.82) * mm, "end": v(29.25, -13.06) * mm});
            skLineSegment(sketch, "E340", {"start": v(29.25, -13.06) * mm, "end": v(29, -13.28) * mm});
            skLineSegment(sketch, "E341", {"start": v(29, -13.28) * mm, "end": v(28.73, -13.5) * mm});
            skLineSegment(sketch, "E342", {"start": v(28.73, -13.5) * mm, "end": v(28.51, -13.67) * mm});
            skLineSegment(sketch, "E343", {"start": v(28.51, -13.67) * mm, "end": v(27.27, -13.23) * mm});
            skLineSegment(sketch, "E344", {"start": v(27.27, -13.23) * mm, "end": v(26.08, -12.68) * mm});
            skLineSegment(sketch, "E345", {"start": v(26.08, -12.68) * mm, "end": v(26.04, -12.42) * mm});
            skLineSegment(sketch, "E346", {"start": v(26.04, -12.42) * mm, "end": v(26, -12.07) * mm});
            skLineSegment(sketch, "E347", {"start": v(26, -12.07) * mm, "end": v(25.97, -11.73) * mm});
            skLineSegment(sketch, "E348", {"start": v(25.97, -11.73) * mm, "end": v(25.97, -11.4) * mm});
            skLineSegment(sketch, "E349", {"start": v(25.97, -11.4) * mm, "end": v(25.97, -11.07) * mm});
            skLineSegment(sketch, "E350", {"start": v(25.97, -11.07) * mm, "end": v(26, -10.75) * mm});
            skLineSegment(sketch, "E351", {"start": v(26, -10.75) * mm, "end": v(26.04, -10.43) * mm});
            skLineSegment(sketch, "E352", {"start": v(26.04, -10.43) * mm, "end": v(26.1, -10.13) * mm});
            skLineSegment(sketch, "E353", {"start": v(26.1, -10.13) * mm, "end": v(26.18, -9.84) * mm});
            skLineSegment(sketch, "E354", {"start": v(26.18, -9.84) * mm, "end": v(26.28, -9.57) * mm});
            skLineSegment(sketch, "E355", {"start": v(26.28, -9.57) * mm, "end": v(26.43, -9.32) * mm});
            skLineSegment(sketch, "E356", {"start": v(26.43, -9.32) * mm, "end": v(26.57, -9.07) * mm});
            skLineSegment(sketch, "E357", {"start": v(26.57, -9.07) * mm, "end": v(26.64, -8.94) * mm});
            skLineSegment(sketch, "E358", {"start": v(26.64, -8.94) * mm, "end": v(26.69, -8.8) * mm});
            skLineSegment(sketch, "E359", {"start": v(26.69, -8.8) * mm, "end": v(26.73, -8.66) * mm});
            skLineSegment(sketch, "E360", {"start": v(26.73, -8.66) * mm, "end": v(26.75, -8.5) * mm});
            skLineSegment(sketch, "E361", {"start": v(26.75, -8.5) * mm, "end": v(26.76, -8.42) * mm});
            skLineSegment(sketch, "E362", {"start": v(26.76, -8.42) * mm, "end": v(26.76, -8.33) * mm});
            skLineSegment(sketch, "E363", {"start": v(26.76, -8.33) * mm, "end": v(26.74, -8.23) * mm});
            skLineSegment(sketch, "E364", {"start": v(26.74, -8.23) * mm, "end": v(26.7, -8.12) * mm});
            skLineSegment(sketch, "E365", {"start": v(26.7, -8.12) * mm, "end": v(26.56, -7.92) * mm});
            skLineSegment(sketch, "E366", {"start": v(26.56, -7.92) * mm, "end": v(25.73, -7.25) * mm});
            skLineSegment(sketch, "E367", {"start": v(25.73, -7.25) * mm, "end": v(24.97, -6.5) * mm});
            skLineSegment(sketch, "E368", {"start": v(24.97, -6.5) * mm, "end": v(24.76, -6.37) * mm});
            skLineSegment(sketch, "E369", {"start": v(24.76, -6.37) * mm, "end": v(24.65, -6.35) * mm});
            skLineSegment(sketch, "E370", {"start": v(24.65, -6.35) * mm, "end": v(24.55, -6.34) * mm});
            skLineSegment(sketch, "E371", {"start": v(24.55, -6.34) * mm, "end": v(24.46, -6.35) * mm});
            skLineSegment(sketch, "E372", {"start": v(24.46, -6.35) * mm, "end": v(24.38, -6.36) * mm});
            skLineSegment(sketch, "E373", {"start": v(24.38, -6.36) * mm, "end": v(24.23, -6.4) * mm});
            skLineSegment(sketch, "E374", {"start": v(24.23, -6.4) * mm, "end": v(24.09, -6.46) * mm});
            skLineSegment(sketch, "E375", {"start": v(24.09, -6.46) * mm, "end": v(23.96, -6.53) * mm});
            skLineSegment(sketch, "E376", {"start": v(23.96, -6.53) * mm, "end": v(23.83, -6.6) * mm});
            skLineSegment(sketch, "E377", {"start": v(23.83, -6.6) * mm, "end": v(23.6, -6.77) * mm});
            skLineSegment(sketch, "E378", {"start": v(23.6, -6.77) * mm, "end": v(23.37, -6.95) * mm});
            skLineSegment(sketch, "E379", {"start": v(23.37, -6.95) * mm, "end": v(23.1, -7.08) * mm});
            skLineSegment(sketch, "E380", {"start": v(23.1, -7.08) * mm, "end": v(22.83, -7.19) * mm});
            skLineSegment(sketch, "E381", {"start": v(22.83, -7.19) * mm, "end": v(22.53, -7.28) * mm});
            skLineSegment(sketch, "E382", {"start": v(22.53, -7.28) * mm, "end": v(22.23, -7.35) * mm});
            skLineSegment(sketch, "E383", {"start": v(22.23, -7.35) * mm, "end": v(21.9, -7.4) * mm});
            skLineSegment(sketch, "E384", {"start": v(21.9, -7.4) * mm, "end": v(21.58, -7.45) * mm});
            skLineSegment(sketch, "E385", {"start": v(21.58, -7.45) * mm, "end": v(21.25, -7.48) * mm});
            skLineSegment(sketch, "E386", {"start": v(21.25, -7.48) * mm, "end": v(20.9, -7.49) * mm});
            skLineSegment(sketch, "E387", {"start": v(20.9, -7.49) * mm, "end": v(20.56, -7.49) * mm});
            skLineSegment(sketch, "E388", {"start": v(20.56, -7.49) * mm, "end": v(20.3, -7.47) * mm});
            skLineSegment(sketch, "E389", {"start": v(20.3, -7.47) * mm, "end": v(19.62, -6.34) * mm});
            skLineSegment(sketch, "E390", {"start": v(19.62, -6.34) * mm, "end": v(19.06, -5.15) * mm});
            skLineSegment(sketch, "E391", {"start": v(19.06, -5.15) * mm, "end": v(19.2, -4.93) * mm});
            skLineSegment(sketch, "E392", {"start": v(19.2, -4.93) * mm, "end": v(19.39, -4.63) * mm});
            skLineSegment(sketch, "E393", {"start": v(19.39, -4.63) * mm, "end": v(19.59, -4.36) * mm});
            skLineSegment(sketch, "E394", {"start": v(19.59, -4.36) * mm, "end": v(19.8, -4.1) * mm});
            skLineSegment(sketch, "E395", {"start": v(19.8, -4.1) * mm, "end": v(20.02, -3.85) * mm});
            skLineSegment(sketch, "E396", {"start": v(20.02, -3.85) * mm, "end": v(20.24, -3.62) * mm});
            skLineSegment(sketch, "E397", {"start": v(20.24, -3.62) * mm, "end": v(20.47, -3.4) * mm});
            skLineSegment(sketch, "E398", {"start": v(20.47, -3.4) * mm, "end": v(20.71, -3.21) * mm});
            skLineSegment(sketch, "E399", {"start": v(20.71, -3.21) * mm, "end": v(20.96, -3.04) * mm});
            skLineSegment(sketch, "E400", {"start": v(20.96, -3.04) * mm, "end": v(21.22, -2.9) * mm});
            skLineSegment(sketch, "E401", {"start": v(21.22, -2.9) * mm, "end": v(21.49, -2.8) * mm});
            skLineSegment(sketch, "E402", {"start": v(21.49, -2.8) * mm, "end": v(21.76, -2.7) * mm});
            skLineSegment(sketch, "E403", {"start": v(21.76, -2.7) * mm, "end": v(21.9, -2.64) * mm});
            skLineSegment(sketch, "E404", {"start": v(21.9, -2.64) * mm, "end": v(22.02, -2.57) * mm});
            skLineSegment(sketch, "E405", {"start": v(22.02, -2.57) * mm, "end": v(22.14, -2.49) * mm});
            skLineSegment(sketch, "E406", {"start": v(22.14, -2.49) * mm, "end": v(22.26, -2.38) * mm});
            skLineSegment(sketch, "E407", {"start": v(22.26, -2.38) * mm, "end": v(22.32, -2.32) * mm});
            skLineSegment(sketch, "E408", {"start": v(22.32, -2.32) * mm, "end": v(22.38, -2.25) * mm});
            skLineSegment(sketch, "E409", {"start": v(22.38, -2.25) * mm, "end": v(22.43, -2.17) * mm});
            skLineSegment(sketch, "E410", {"start": v(22.43, -2.17) * mm, "end": v(22.47, -2.06) * mm});
            skLineSegment(sketch, "E411", {"start": v(22.47, -2.06) * mm, "end": v(22.48, -1.82) * mm});
            skLineSegment(sketch, "E412", {"start": v(22.48, -1.82) * mm, "end": v(22.28, -0.77) * mm});
            skLineSegment(sketch, "E413", {"start": v(22.28, -0.77) * mm, "end": v(22.19, 0.3) * mm});
            skCircle(sketch, "E414", {"center": v(32.91, 0.73) * mm, "radius": 3 * mm});
            skSolve(sketch);
        }
        {
            var Q0;
            Q0=makeQuery(id+"F0.imprint","IMPRINT",FACE,{"disambiguationData":[TD([[makeQuery(id+"F0.imprint","IMPRINT",EDGE,{"derivedFrom":sQuery(id+"F0.wireOp",EDGE,"E0")}),-1.0]])]});
            extrude(context, id + "F1", {"entities" : qUnion([Q0]), "depth" : 10 * mm, "offsetDistance" : 25 * mm});
        }
        {
            var Q0;
            Q0=makeQuery(id+"F1.opExtrude","CAP_FACE",FACE,{"disambiguationData":[OSD([sQuery(id+"F0.wireOp",EDGE,"E0"),sQuery(id+"F0.wireOp",EDGE,"E1"),sQuery(id+"F0.wireOp",EDGE,"E2"),sQuery(id+"F0.wireOp",EDGE,"E3"),sQuery(id+"F0.wireOp",EDGE,"E4"),sQuery(id+"F0.wireOp",EDGE,"E5"),sQuery(id+"F0.wireOp",EDGE,"E6"),sQuery(id+"F0.wireOp",EDGE,"E7"),sQuery(id+"F0.wireOp",EDGE,"E8"),sQuery(id+"F0.wireOp",EDGE,"E9"),sQuery(id+"F0.wireOp",EDGE,"E10"),sQuery(id+"F0.wireOp",EDGE,"E11"),sQuery(id+"F0.wireOp",EDGE,"E12"),sQuery(id+"F0.wireOp",EDGE,"E13"),sQuery(id+"F0.wireOp",EDGE,"E14"),sQuery(id+"F0.wireOp",EDGE,"E15"),sQuery(id+"F0.wireOp",EDGE,"E16"),sQuery(id+"F0.wireOp",EDGE,"E17"),sQuery(id+"F0.wireOp",EDGE,"E18"),sQuery(id+"F0.wireOp",EDGE,"E19"),sQuery(id+"F0.wireOp",EDGE,"E20"),sQuery(id+"F0.wireOp",EDGE,"E21"),sQuery(id+"F0.wireOp",EDGE,"E22"),sQuery(id+"F0.wireOp",EDGE,"E23"),sQuery(id+"F0.wireOp",EDGE,"E24"),sQuery(id+"F0.wireOp",EDGE,"E25"),sQuery(id+"F0.wireOp",EDGE,"E26"),sQuery(id+"F0.wireOp",EDGE,"E27"),sQuery(id+"F0.wireOp",EDGE,"E28"),sQuery(id+"F0.wireOp",EDGE,"E29"),sQuery(id+"F0.wireOp",EDGE,"E30"),sQuery(id+"F0.wireOp",EDGE,"E31"),sQuery(id+"F0.wireOp",EDGE,"E32"),sQuery(id+"F0.wireOp",EDGE,"E33"),sQuery(id+"F0.wireOp",EDGE,"E34"),sQuery(id+"F0.wireOp",EDGE,"E35"),sQuery(id+"F0.wireOp",EDGE,"E36"),sQuery(id+"F0.wireOp",EDGE,"E37"),sQuery(id+"F0.wireOp",EDGE,"E38"),sQuery(id+"F0.wireOp",EDGE,"E39"),sQuery(id+"F0.wireOp",EDGE,"E40"),sQuery(id+"F0.wireOp",EDGE,"E41"),sQuery(id+"F0.wireOp",EDGE,"E42"),sQuery(id+"F0.wireOp",EDGE,"E43"),sQuery(id+"F0.wireOp",EDGE,"E44"),sQuery(id+"F0.wireOp",EDGE,"E45"),sQuery(id+"F0.wireOp",EDGE,"E46"),sQuery(id+"F0.wireOp",EDGE,"E47"),sQuery(id+"F0.wireOp",EDGE,"E48"),sQuery(id+"F0.wireOp",EDGE,"E49"),sQuery(id+"F0.wireOp",EDGE,"E50"),sQuery(id+"F0.wireOp",EDGE,"E51"),sQuery(id+"F0.wireOp",EDGE,"E52"),sQuery(id+"F0.wireOp",EDGE,"E53"),sQuery(id+"F0.wireOp",EDGE,"E54"),sQuery(id+"F0.wireOp",EDGE,"E55"),sQuery(id+"F0.wireOp",EDGE,"E56"),sQuery(id+"F0.wireOp",EDGE,"E57"),sQuery(id+"F0.wireOp",EDGE,"E58"),sQuery(id+"F0.wireOp",EDGE,"E59"),sQuery(id+"F0.wireOp",EDGE,"E60"),sQuery(id+"F0.wireOp",EDGE,"E61"),sQuery(id+"F0.wireOp",EDGE,"E62"),sQuery(id+"F0.wireOp",EDGE,"E63"),sQuery(id+"F0.wireOp",EDGE,"E64"),sQuery(id+"F0.wireOp",EDGE,"E65"),sQuery(id+"F0.wireOp",EDGE,"E66"),sQuery(id+"F0.wireOp",EDGE,"E67"),sQuery(id+"F0.wireOp",EDGE,"E68"),sQuery(id+"F0.wireOp",EDGE,"E69"),sQuery(id+"F0.wireOp",EDGE,"E70"),sQuery(id+"F0.wireOp",EDGE,"E71"),sQuery(id+"F0.wireOp",EDGE,"E72"),sQuery(id+"F0.wireOp",EDGE,"E73"),sQuery(id+"F0.wireOp",EDGE,"E74"),sQuery(id+"F0.wireOp",EDGE,"E75"),sQuery(id+"F0.wireOp",EDGE,"E76"),sQuery(id+"F0.wireOp",EDGE,"E77"),sQuery(id+"F0.wireOp",EDGE,"E78"),sQuery(id+"F0.wireOp",EDGE,"E79"),sQuery(id+"F0.wireOp",EDGE,"E80"),sQuery(id+"F0.wireOp",EDGE,"E81"),sQuery(id+"F0.wireOp",EDGE,"E82"),sQuery(id+"F0.wireOp",EDGE,"E83"),sQuery(id+"F0.wireOp",EDGE,"E84"),sQuery(id+"F0.wireOp",EDGE,"E85"),sQuery(id+"F0.wireOp",EDGE,"E86"),sQuery(id+"F0.wireOp",EDGE,"E87"),sQuery(id+"F0.wireOp",EDGE,"E88"),sQuery(id+"F0.wireOp",EDGE,"E89"),sQuery(id+"F0.wireOp",EDGE,"E90"),sQuery(id+"F0.wireOp",EDGE,"E91"),sQuery(id+"F0.wireOp",EDGE,"E92"),sQuery(id+"F0.wireOp",EDGE,"E93"),sQuery(id+"F0.wireOp",EDGE,"E94"),sQuery(id+"F0.wireOp",EDGE,"E95"),sQuery(id+"F0.wireOp",EDGE,"E96"),sQuery(id+"F0.wireOp",EDGE,"E97"),sQuery(id+"F0.wireOp",EDGE,"E98"),sQuery(id+"F0.wireOp",EDGE,"E99"),sQuery(id+"F0.wireOp",EDGE,"E100"),sQuery(id+"F0.wireOp",EDGE,"E101"),sQuery(id+"F0.wireOp",EDGE,"E102"),sQuery(id+"F0.wireOp",EDGE,"E103"),sQuery(id+"F0.wireOp",EDGE,"E104"),sQuery(id+"F0.wireOp",EDGE,"E105"),sQuery(id+"F0.wireOp",EDGE,"E106"),sQuery(id+"F0.wireOp",EDGE,"E107"),sQuery(id+"F0.wireOp",EDGE,"E108"),sQuery(id+"F0.wireOp",EDGE,"E109"),sQuery(id+"F0.wireOp",EDGE,"E110"),sQuery(id+"F0.wireOp",EDGE,"E111"),sQuery(id+"F0.wireOp",EDGE,"E112"),sQuery(id+"F0.wireOp",EDGE,"E113"),sQuery(id+"F0.wireOp",EDGE,"E114"),sQuery(id+"F0.wireOp",EDGE,"E115"),sQuery(id+"F0.wireOp",EDGE,"E116"),sQuery(id+"F0.wireOp",EDGE,"E117"),sQuery(id+"F0.wireOp",EDGE,"E118"),sQuery(id+"F0.wireOp",EDGE,"E119"),sQuery(id+"F0.wireOp",EDGE,"E120"),sQuery(id+"F0.wireOp",EDGE,"E121"),sQuery(id+"F0.wireOp",EDGE,"E122"),sQuery(id+"F0.wireOp",EDGE,"E123"),sQuery(id+"F0.wireOp",EDGE,"E124"),sQuery(id+"F0.wireOp",EDGE,"E125"),sQuery(id+"F0.wireOp",EDGE,"E126"),sQuery(id+"F0.wireOp",EDGE,"E127"),sQuery(id+"F0.wireOp",EDGE,"E128"),sQuery(id+"F0.wireOp",EDGE,"E129"),sQuery(id+"F0.wireOp",EDGE,"E130"),sQuery(id+"F0.wireOp",EDGE,"E131"),sQuery(id+"F0.wireOp",EDGE,"E132"),sQuery(id+"F0.wireOp",EDGE,"E133"),sQuery(id+"F0.wireOp",EDGE,"E134"),sQuery(id+"F0.wireOp",EDGE,"E135"),sQuery(id+"F0.wireOp",EDGE,"E136"),sQuery(id+"F0.wireOp",EDGE,"E137"),sQuery(id+"F0.wireOp",EDGE,"E138"),sQuery(id+"F0.wireOp",EDGE,"E139"),sQuery(id+"F0.wireOp",EDGE,"E140"),sQuery(id+"F0.wireOp",EDGE,"E141"),sQuery(id+"F0.wireOp",EDGE,"E142"),sQuery(id+"F0.wireOp",EDGE,"E143"),sQuery(id+"F0.wireOp",EDGE,"E144"),sQuery(id+"F0.wireOp",EDGE,"E145"),sQuery(id+"F0.wireOp",EDGE,"E146"),sQuery(id+"F0.wireOp",EDGE,"E147"),sQuery(id+"F0.wireOp",EDGE,"E148"),sQuery(id+"F0.wireOp",EDGE,"E149"),sQuery(id+"F0.wireOp",EDGE,"E150"),sQuery(id+"F0.wireOp",EDGE,"E151"),sQuery(id+"F0.wireOp",EDGE,"E152"),sQuery(id+"F0.wireOp",EDGE,"E153"),sQuery(id+"F0.wireOp",EDGE,"E154"),sQuery(id+"F0.wireOp",EDGE,"E155"),sQuery(id+"F0.wireOp",EDGE,"E156"),sQuery(id+"F0.wireOp",EDGE,"E157"),sQuery(id+"F0.wireOp",EDGE,"E158"),sQuery(id+"F0.wireOp",EDGE,"E159"),sQuery(id+"F0.wireOp",EDGE,"E160"),sQuery(id+"F0.wireOp",EDGE,"E161"),sQuery(id+"F0.wireOp",EDGE,"E162"),sQuery(id+"F0.wireOp",EDGE,"E163"),sQuery(id+"F0.wireOp",EDGE,"E164"),sQuery(id+"F0.wireOp",EDGE,"E165"),sQuery(id+"F0.wireOp",EDGE,"E166"),sQuery(id+"F0.wireOp",EDGE,"E167"),sQuery(id+"F0.wireOp",EDGE,"E168"),sQuery(id+"F0.wireOp",EDGE,"E169"),sQuery(id+"F0.wireOp",EDGE,"E170"),sQuery(id+"F0.wireOp",EDGE,"E171"),sQuery(id+"F0.wireOp",EDGE,"E172"),sQuery(id+"F0.wireOp",EDGE,"E173"),sQuery(id+"F0.wireOp",EDGE,"E174"),sQuery(id+"F0.wireOp",EDGE,"E175"),sQuery(id+"F0.wireOp",EDGE,"E176"),sQuery(id+"F0.wireOp",EDGE,"E177"),sQuery(id+"F0.wireOp",EDGE,"E178"),sQuery(id+"F0.wireOp",EDGE,"E179"),sQuery(id+"F0.wireOp",EDGE,"E180"),sQuery(id+"F0.wireOp",EDGE,"E181"),sQuery(id+"F0.wireOp",EDGE,"E182"),sQuery(id+"F0.wireOp",EDGE,"E183"),sQuery(id+"F0.wireOp",EDGE,"E184"),sQuery(id+"F0.wireOp",EDGE,"E185"),sQuery(id+"F0.wireOp",EDGE,"E186"),sQuery(id+"F0.wireOp",EDGE,"E187"),sQuery(id+"F0.wireOp",EDGE,"E188"),sQuery(id+"F0.wireOp",EDGE,"E189"),sQuery(id+"F0.wireOp",EDGE,"E190"),sQuery(id+"F0.wireOp",EDGE,"E191"),sQuery(id+"F0.wireOp",EDGE,"E192"),sQuery(id+"F0.wireOp",EDGE,"E193"),sQuery(id+"F0.wireOp",EDGE,"E194"),sQuery(id+"F0.wireOp",EDGE,"E195"),sQuery(id+"F0.wireOp",EDGE,"E196"),sQuery(id+"F0.wireOp",EDGE,"E197"),sQuery(id+"F0.wireOp",EDGE,"E198"),sQuery(id+"F0.wireOp",EDGE,"E199"),sQuery(id+"F0.wireOp",EDGE,"E200"),sQuery(id+"F0.wireOp",EDGE,"E201"),sQuery(id+"F0.wireOp",EDGE,"E202"),sQuery(id+"F0.wireOp",EDGE,"E203"),sQuery(id+"F0.wireOp",EDGE,"E204"),sQuery(id+"F0.wireOp",EDGE,"E205"),sQuery(id+"F0.wireOp",EDGE,"E206"),sQuery(id+"F0.wireOp",EDGE,"E207"),sQuery(id+"F0.wireOp",EDGE,"E208"),sQuery(id+"F0.wireOp",EDGE,"E209"),sQuery(id+"F0.wireOp",EDGE,"E210"),sQuery(id+"F0.wireOp",EDGE,"E211"),sQuery(id+"F0.wireOp",EDGE,"E212"),sQuery(id+"F0.wireOp",EDGE,"E213"),sQuery(id+"F0.wireOp",EDGE,"E214"),sQuery(id+"F0.wireOp",EDGE,"E215"),sQuery(id+"F0.wireOp",EDGE,"E216"),sQuery(id+"F0.wireOp",EDGE,"E217"),sQuery(id+"F0.wireOp",EDGE,"E218"),sQuery(id+"F0.wireOp",EDGE,"E219"),sQuery(id+"F0.wireOp",EDGE,"E220"),sQuery(id+"F0.wireOp",EDGE,"E221"),sQuery(id+"F0.wireOp",EDGE,"E222"),sQuery(id+"F0.wireOp",EDGE,"E223"),sQuery(id+"F0.wireOp",EDGE,"E224"),sQuery(id+"F0.wireOp",EDGE,"E225"),sQuery(id+"F0.wireOp",EDGE,"E226"),sQuery(id+"F0.wireOp",EDGE,"E227"),sQuery(id+"F0.wireOp",EDGE,"E228"),sQuery(id+"F0.wireOp",EDGE,"E229"),sQuery(id+"F0.wireOp",EDGE,"E230"),sQuery(id+"F0.wireOp",EDGE,"E231"),sQuery(id+"F0.wireOp",EDGE,"E232"),sQuery(id+"F0.wireOp",EDGE,"E233"),sQuery(id+"F0.wireOp",EDGE,"E234"),sQuery(id+"F0.wireOp",EDGE,"E235"),sQuery(id+"F0.wireOp",EDGE,"E236"),sQuery(id+"F0.wireOp",EDGE,"E237"),sQuery(id+"F0.wireOp",EDGE,"E238"),sQuery(id+"F0.wireOp",EDGE,"E239"),sQuery(id+"F0.wireOp",EDGE,"E240"),sQuery(id+"F0.wireOp",EDGE,"E241"),sQuery(id+"F0.wireOp",EDGE,"E242"),sQuery(id+"F0.wireOp",EDGE,"E243"),sQuery(id+"F0.wireOp",EDGE,"E244"),sQuery(id+"F0.wireOp",EDGE,"E245"),sQuery(id+"F0.wireOp",EDGE,"E246"),sQuery(id+"F0.wireOp",EDGE,"E247"),sQuery(id+"F0.wireOp",EDGE,"E248"),sQuery(id+"F0.wireOp",EDGE,"E249"),sQuery(id+"F0.wireOp",EDGE,"E250"),sQuery(id+"F0.wireOp",EDGE,"E251"),sQuery(id+"F0.wireOp",EDGE,"E252"),sQuery(id+"F0.wireOp",EDGE,"E253"),sQuery(id+"F0.wireOp",EDGE,"E254"),sQuery(id+"F0.wireOp",EDGE,"E255"),sQuery(id+"F0.wireOp",EDGE,"E256"),sQuery(id+"F0.wireOp",EDGE,"E257"),sQuery(id+"F0.wireOp",EDGE,"E258"),sQuery(id+"F0.wireOp",EDGE,"E259"),sQuery(id+"F0.wireOp",EDGE,"E260"),sQuery(id+"F0.wireOp",EDGE,"E261"),sQuery(id+"F0.wireOp",EDGE,"E262"),sQuery(id+"F0.wireOp",EDGE,"E263"),sQuery(id+"F0.wireOp",EDGE,"E264"),sQuery(id+"F0.wireOp",EDGE,"E265"),sQuery(id+"F0.wireOp",EDGE,"E266"),sQuery(id+"F0.wireOp",EDGE,"E267"),sQuery(id+"F0.wireOp",EDGE,"E268"),sQuery(id+"F0.wireOp",EDGE,"E269"),sQuery(id+"F0.wireOp",EDGE,"E270"),sQuery(id+"F0.wireOp",EDGE,"E271"),sQuery(id+"F0.wireOp",EDGE,"E272"),sQuery(id+"F0.wireOp",EDGE,"E273"),sQuery(id+"F0.wireOp",EDGE,"E274"),sQuery(id+"F0.wireOp",EDGE,"E275"),sQuery(id+"F0.wireOp",EDGE,"E276"),sQuery(id+"F0.wireOp",EDGE,"E277"),sQuery(id+"F0.wireOp",EDGE,"E278"),sQuery(id+"F0.wireOp",EDGE,"E279"),sQuery(id+"F0.wireOp",EDGE,"E280"),sQuery(id+"F0.wireOp",EDGE,"E281"),sQuery(id+"F0.wireOp",EDGE,"E282"),sQuery(id+"F0.wireOp",EDGE,"E283"),sQuery(id+"F0.wireOp",EDGE,"E284"),sQuery(id+"F0.wireOp",EDGE,"E285"),sQuery(id+"F0.wireOp",EDGE,"E286"),sQuery(id+"F0.wireOp",EDGE,"E287"),sQuery(id+"F0.wireOp",EDGE,"E288"),sQuery(id+"F0.wireOp",EDGE,"E289"),sQuery(id+"F0.wireOp",EDGE,"E290"),sQuery(id+"F0.wireOp",EDGE,"E291"),sQuery(id+"F0.wireOp",EDGE,"E292"),sQuery(id+"F0.wireOp",EDGE,"E293"),sQuery(id+"F0.wireOp",EDGE,"E294"),sQuery(id+"F0.wireOp",EDGE,"E295"),sQuery(id+"F0.wireOp",EDGE,"E296"),sQuery(id+"F0.wireOp",EDGE,"E297"),sQuery(id+"F0.wireOp",EDGE,"E298"),sQuery(id+"F0.wireOp",EDGE,"E299"),sQuery(id+"F0.wireOp",EDGE,"E300"),sQuery(id+"F0.wireOp",EDGE,"E301"),sQuery(id+"F0.wireOp",EDGE,"E302"),sQuery(id+"F0.wireOp",EDGE,"E303"),sQuery(id+"F0.wireOp",EDGE,"E304"),sQuery(id+"F0.wireOp",EDGE,"E305"),sQuery(id+"F0.wireOp",EDGE,"E306"),sQuery(id+"F0.wireOp",EDGE,"E307"),sQuery(id+"F0.wireOp",EDGE,"E308"),sQuery(id+"F0.wireOp",EDGE,"E309"),sQuery(id+"F0.wireOp",EDGE,"E310"),sQuery(id+"F0.wireOp",EDGE,"E311"),sQuery(id+"F0.wireOp",EDGE,"E312"),sQuery(id+"F0.wireOp",EDGE,"E313"),sQuery(id+"F0.wireOp",EDGE,"E314"),sQuery(id+"F0.wireOp",EDGE,"E315"),sQuery(id+"F0.wireOp",EDGE,"E316"),sQuery(id+"F0.wireOp",EDGE,"E317"),sQuery(id+"F0.wireOp",EDGE,"E318"),sQuery(id+"F0.wireOp",EDGE,"E319"),sQuery(id+"F0.wireOp",EDGE,"E320"),sQuery(id+"F0.wireOp",EDGE,"E321"),sQuery(id+"F0.wireOp",EDGE,"E322"),sQuery(id+"F0.wireOp",EDGE,"E323"),sQuery(id+"F0.wireOp",EDGE,"E324"),sQuery(id+"F0.wireOp",EDGE,"E325"),sQuery(id+"F0.wireOp",EDGE,"E326"),sQuery(id+"F0.wireOp",EDGE,"E327"),sQuery(id+"F0.wireOp",EDGE,"E328"),sQuery(id+"F0.wireOp",EDGE,"E329"),sQuery(id+"F0.wireOp",EDGE,"E330"),sQuery(id+"F0.wireOp",EDGE,"E331"),sQuery(id+"F0.wireOp",EDGE,"E332"),sQuery(id+"F0.wireOp",EDGE,"E333"),sQuery(id+"F0.wireOp",EDGE,"E334"),sQuery(id+"F0.wireOp",EDGE,"E335"),sQuery(id+"F0.wireOp",EDGE,"E336"),sQuery(id+"F0.wireOp",EDGE,"E337"),sQuery(id+"F0.wireOp",EDGE,"E338"),sQuery(id+"F0.wireOp",EDGE,"E339"),sQuery(id+"F0.wireOp",EDGE,"E340"),sQuery(id+"F0.wireOp",EDGE,"E341"),sQuery(id+"F0.wireOp",EDGE,"E342"),sQuery(id+"F0.wireOp",EDGE,"E343"),sQuery(id+"F0.wireOp",EDGE,"E344"),sQuery(id+"F0.wireOp",EDGE,"E345"),sQuery(id+"F0.wireOp",EDGE,"E346"),sQuery(id+"F0.wireOp",EDGE,"E347"),sQuery(id+"F0.wireOp",EDGE,"E348"),sQuery(id+"F0.wireOp",EDGE,"E349"),sQuery(id+"F0.wireOp",EDGE,"E350"),sQuery(id+"F0.wireOp",EDGE,"E351"),sQuery(id+"F0.wireOp",EDGE,"E352"),sQuery(id+"F0.wireOp",EDGE,"E353"),sQuery(id+"F0.wireOp",EDGE,"E354"),sQuery(id+"F0.wireOp",EDGE,"E355"),sQuery(id+"F0.wireOp",EDGE,"E356"),sQuery(id+"F0.wireOp",EDGE,"E357"),sQuery(id+"F0.wireOp",EDGE,"E358"),sQuery(id+"F0.wireOp",EDGE,"E359"),sQuery(id+"F0.wireOp",EDGE,"E360"),sQuery(id+"F0.wireOp",EDGE,"E361"),sQuery(id+"F0.wireOp",EDGE,"E362"),sQuery(id+"F0.wireOp",EDGE,"E363"),sQuery(id+"F0.wireOp",EDGE,"E364"),sQuery(id+"F0.wireOp",EDGE,"E365"),sQuery(id+"F0.wireOp",EDGE,"E366"),sQuery(id+"F0.wireOp",EDGE,"E367"),sQuery(id+"F0.wireOp",EDGE,"E368"),sQuery(id+"F0.wireOp",EDGE,"E369"),sQuery(id+"F0.wireOp",EDGE,"E370"),sQuery(id+"F0.wireOp",EDGE,"E371"),sQuery(id+"F0.wireOp",EDGE,"E372"),sQuery(id+"F0.wireOp",EDGE,"E373"),sQuery(id+"F0.wireOp",EDGE,"E374"),sQuery(id+"F0.wireOp",EDGE,"E375"),sQuery(id+"F0.wireOp",EDGE,"E376"),sQuery(id+"F0.wireOp",EDGE,"E377"),sQuery(id+"F0.wireOp",EDGE,"E378"),sQuery(id+"F0.wireOp",EDGE,"E379"),sQuery(id+"F0.wireOp",EDGE,"E380"),sQuery(id+"F0.wireOp",EDGE,"E381"),sQuery(id+"F0.wireOp",EDGE,"E382"),sQuery(id+"F0.wireOp",EDGE,"E383"),sQuery(id+"F0.wireOp",EDGE,"E384"),sQuery(id+"F0.wireOp",EDGE,"E385"),sQuery(id+"F0.wireOp",EDGE,"E386"),sQuery(id+"F0.wireOp",EDGE,"E387"),sQuery(id+"F0.wireOp",EDGE,"E388"),sQuery(id+"F0.wireOp",EDGE,"E389"),sQuery(id+"F0.wireOp",EDGE,"E390"),sQuery(id+"F0.wireOp",EDGE,"E391"),sQuery(id+"F0.wireOp",EDGE,"E392"),sQuery(id+"F0.wireOp",EDGE,"E393"),sQuery(id+"F0.wireOp",EDGE,"E394"),sQuery(id+"F0.wireOp",EDGE,"E395"),sQuery(id+"F0.wireOp",EDGE,"E396"),sQuery(id+"F0.wireOp",EDGE,"E397"),sQuery(id+"F0.wireOp",EDGE,"E398"),sQuery(id+"F0.wireOp",EDGE,"E399"),sQuery(id+"F0.wireOp",EDGE,"E400"),sQuery(id+"F0.wireOp",EDGE,"E401"),sQuery(id+"F0.wireOp",EDGE,"E402"),sQuery(id+"F0.wireOp",EDGE,"E403"),sQuery(id+"F0.wireOp",EDGE,"E404"),sQuery(id+"F0.wireOp",EDGE,"E405"),sQuery(id+"F0.wireOp",EDGE,"E406"),sQuery(id+"F0.wireOp",EDGE,"E407"),sQuery(id+"F0.wireOp",EDGE,"E408"),sQuery(id+"F0.wireOp",EDGE,"E409"),sQuery(id+"F0.wireOp",EDGE,"E410"),sQuery(id+"F0.wireOp",EDGE,"E411"),sQuery(id+"F0.wireOp",EDGE,"E412"),sQuery(id+"F0.wireOp",EDGE,"E413"),sQuery(id+"F0.wireOp",EDGE,"E414")])],"isStart":false});
            var sketch = newSketch(context, id + "F2", { "sketchPlane" : qUnion([Q0])});
            skCircle(sketch, "E415", {"center": v(32.91, 0.73) * mm, "radius": 4 * mm});
            skCircle(sketch, "E416", {"center": v(32.91, 0.73) * mm, "radius": 9 * mm});
            skSolve(sketch);
        }
        {
            var Q0;
            Q0=makeQuery(id+"F2.imprint","IMPRINT",FACE,{"disambiguationData":[TD([[makeQuery(id+"F2.imprint","IMPRINT",EDGE,{"derivedFrom":sQuery(id+"F2.wireOp",EDGE,"E415")}),-1.0]])]});
            extrude(context, id + "F3", {"entities" : qUnion([Q0]), "operationType" : NewBodyOperationType.REMOVE, "oppositeDirection" : true, "depth" : 4 * mm, "offsetDistance" : 25 * mm});
        }
        {
            var Q0;
            Q0=makeQuery(id+"F3.boolean.opBoolean","COPY",EDGE,{"derivedFrom":makeQuery(id+"F3.opExtrude","CAP_EDGE",EDGE,{"disambiguationData":[OSD([sQuery(id+"F2.wireOp",EDGE,"E416")])],"isStart":false})});
            var Q1;
            Q1=makeQuery(id+"F3.boolean.opBoolean","COPY",EDGE,{"derivedFrom":makeQuery(id+"F3.opExtrude","CAP_EDGE",EDGE,{"disambiguationData":[OSD([sQuery(id+"F2.wireOp",EDGE,"E415")])],"isStart":false})});
            fillet(context, id + "F4", {"entities" : qUnion([Q0, Q1]), "radius" : 1 * mm, "tangentPropagation" : true, "allowEdgeOverflow" : false});
        }
    });
